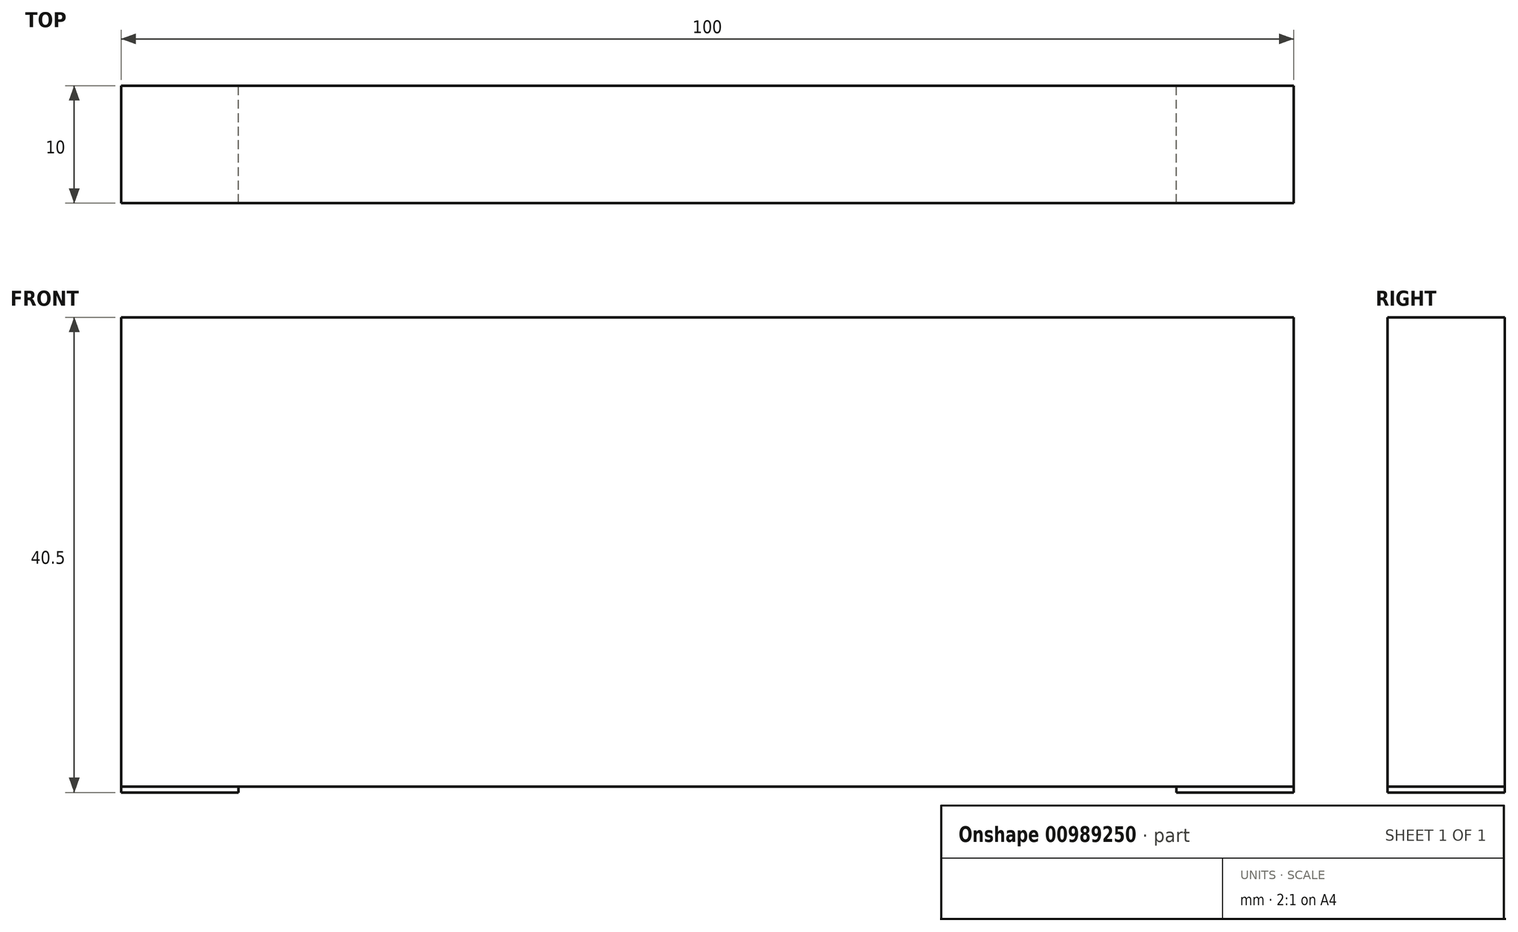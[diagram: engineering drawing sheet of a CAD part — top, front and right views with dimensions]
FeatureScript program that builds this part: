
annotation { "Feature Type Name" : "Feature", "Feature Type Description" : "" }
export const myFeature = defineFeature(function(context is Context, id is Id, definition is map)
    precondition{}
    {
        {
            var Q0;
            Q0=qCreatedBy(makeId("Front.planeOp"),FACE);
            var sketch = newSketch(context, id + "F0", { "sketchPlane" : qUnion([Q0])});
            skLineSegment(sketch, "E0.bottom", {"start": v(-50, 0) * mm, "end": v(50, 0) * mm});
            skLineSegment(sketch, "E0.top", {"start": v(-50, 40) * mm, "end": v(50, 40) * mm});
            skLineSegment(sketch, "E0.left", {"start": v(-50, 0) * mm, "end": v(-50, 40) * mm});
            skLineSegment(sketch, "E0.right", {"start": v(50, 0) * mm, "end": v(50, 40) * mm});
            skSolve(sketch);
        }
        {
            var Q0;
            Q0=makeQuery(id+"F0.imprint","IMPRINT",FACE,{"disambiguationData":[TD([[makeQuery(id+"F0.imprint","IMPRINT",EDGE,{"derivedFrom":sQuery(id+"F0.wireOp",EDGE,"E0.bottom")}),1.0]])]});
            extrude(context, id + "F1", {"entities" : qUnion([Q0]), "depth" : 10 * mm, "offsetDistance" : 25 * mm});
        }
        {
            var Q0;
            Q0=makeQuery(id+"F1.opExtrude","SWEPT_FACE",FACE,{"disambiguationData":[OSD([sQuery(id+"F0.wireOp",EDGE,"E0.bottom")])]});
            var sketch = newSketch(context, id + "F2", { "sketchPlane" : qUnion([Q0])});
            skLineSegment(sketch, "E1.bottom", {"start": v(-50, 10) * mm, "end": v(-40, 10) * mm});
            skLineSegment(sketch, "E1.top", {"start": v(-50, 0) * mm, "end": v(-40, 0) * mm});
            skLineSegment(sketch, "E1.left", {"start": v(-50, 10) * mm, "end": v(-50, 0) * mm});
            skLineSegment(sketch, "E1.right", {"start": v(-40, 10) * mm, "end": v(-40, 0) * mm});
            skLineSegment(sketch, "E2.MirrorCS", {"start": v(50, 0) * mm, "end": v(40, 0) * mm});
            skLineSegment(sketch, "E3.MirrorCS", {"start": v(50, 10) * mm, "end": v(50, 0) * mm});
            skLineSegment(sketch, "E4.MirrorCS", {"start": v(50, 10) * mm, "end": v(40, 10) * mm});
            skLineSegment(sketch, "E5.MirrorCS", {"start": v(40, 10) * mm, "end": v(40, 0) * mm});
            skSolve(sketch);
        }
        {
            var Q0;
            Q0=makeQuery(id+"F2.imprint","IMPRINT",FACE,{"disambiguationData":[TD([[makeQuery(id+"F2.imprint","IMPRINT",EDGE,{"derivedFrom":sQuery(id+"F2.wireOp",EDGE,"E2.MirrorCS")}),1.0]])]});
            var Q1;
            Q1=makeQuery(id+"F2.imprint","IMPRINT",FACE,{"disambiguationData":[TD([[makeQuery(id+"F2.imprint","IMPRINT",EDGE,{"derivedFrom":sQuery(id+"F2.wireOp",EDGE,"E1.bottom")}),-1.0]])]});
            extrude(context, id + "F3", {"entities" : qUnion([Q0, Q1]), "depth" : 0.5 * mm, "offsetDistance" : 25 * mm});
        }
    });
